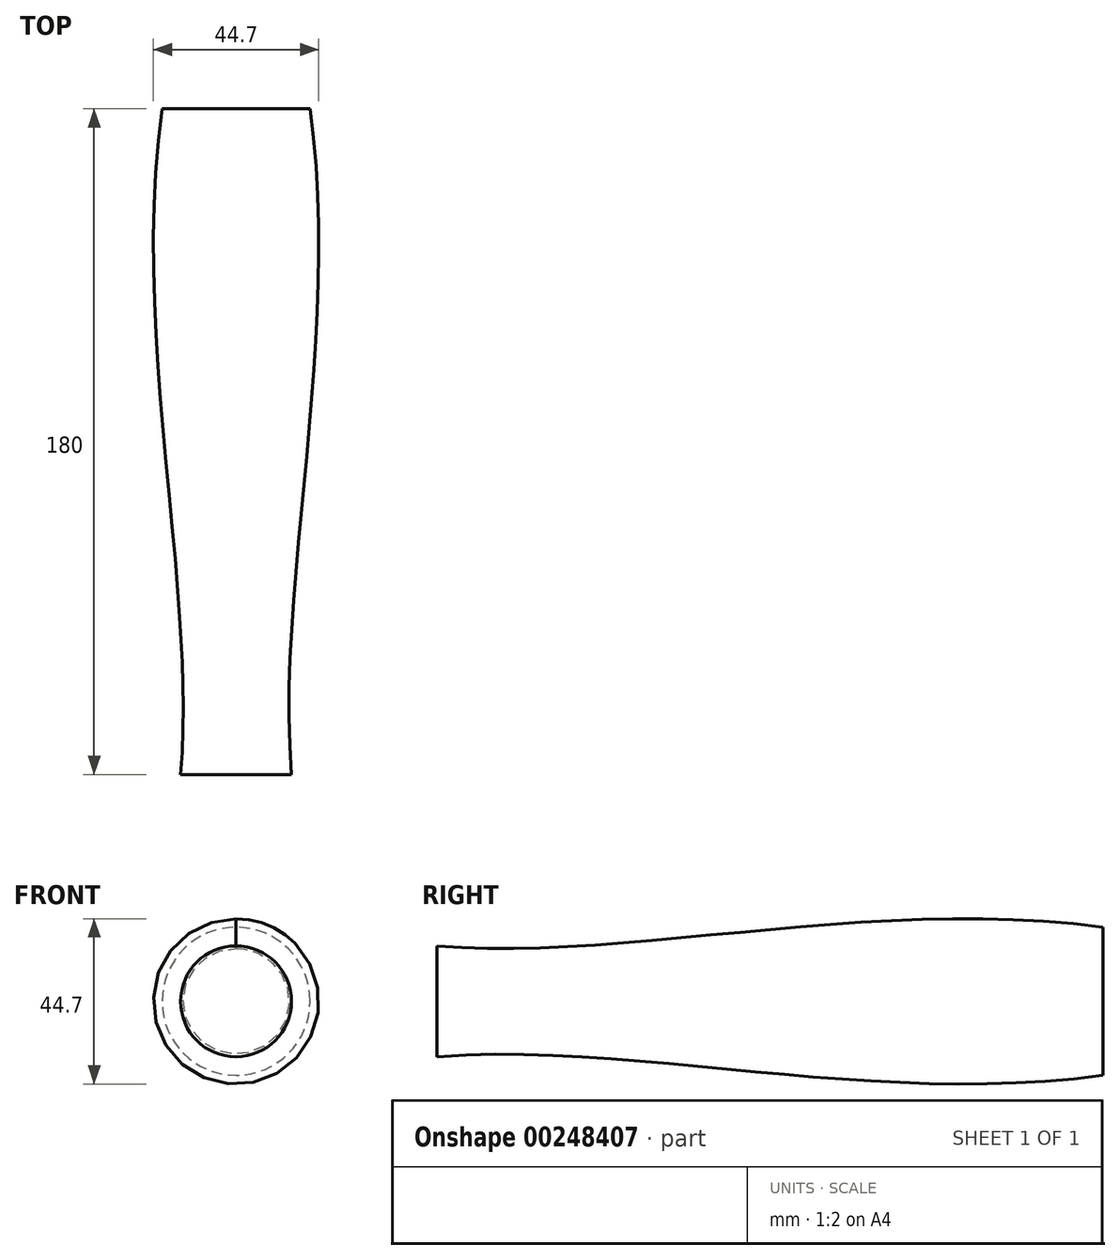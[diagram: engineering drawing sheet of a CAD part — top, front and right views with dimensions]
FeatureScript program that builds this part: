
annotation { "Feature Type Name" : "Feature", "Feature Type Description" : "" }
export const myFeature = defineFeature(function(context is Context, id is Id, definition is map)
    precondition{}
    {
        {
            var Q0;
            Q0=qCreatedBy(makeId("Top.planeOp"),FACE);
            var sketch = newSketch(context, id + "F0", { "sketchPlane" : qUnion([Q0])});
            skLineSegment(sketch, "E0", {"start": v(0, 0) * mm, "end": v(20, 0) * mm});
            skLineSegment(sketch, "E1", {"start": v(0, 0) * mm, "end": v(0, -180) * mm});
            skLineSegment(sketch, "E2", {"start": v(0, -180) * mm, "end": v(15, -180) * mm});
            skFitSpline(sketch, "E3", {"points": [v(15, -180) * mm, v(20, 0) * mm], "startDerivative": vector(-13.26, 151.57) * mm, "endDerivative": vector(-25.76, 183.3) * mm});
            skLineSegment(sketch, "E4", {"start": v(15, -180) * mm, "end": v(15, 0) * mm, "construction": true});
            skLineSegment(sketch, "E5", {"start": v(15, -180) * mm, "end": v(10.58, -129.48) * mm, "construction": true});
            skLineSegment(sketch, "E6", {"start": v(20, 0) * mm, "end": v(28.59, -61.1) * mm, "construction": true});
            skSolve(sketch);
        }
        {
            var Q0;
            Q0=makeQuery(id+"F0.imprint","IMPRINT",FACE,{"disambiguationData":[TD([[makeQuery(id+"F0.imprint","IMPRINT",EDGE,{"derivedFrom":sQuery(id+"F0.wireOp",EDGE,"E0")}),-1.0]])]});
            var Q1;
            Q1=sQuery(id+"F0.wireOp",EDGE,"E1");
            revolve(context, id + "F1", {"entities" : qUnion([Q0]), "axis" : qUnion([Q1]), "revolveType" : RevolveType.FULL});
        }
    });
